# Revit family: LED SERIES
name_source: partatom
category: Lighting Fixtures
units: mm (PartAtom-declared; Revit-internal decimal feet)

## family parameters
Cut with Voids When Loaded = No
Host = Face
Light Source = Yes
OmniClass Number = 23.80.70.11
OmniClass Title = Luminaries for Internal Lighting
Part Type = Normal
Room Calculation Point = No
Round Connector Dimension = Use Diameter
Shared = No

## types (1)
- LED SERIES
    Color Filter = 16777215
    Default Elevation = 48"
    Description = Formed aluminum exit sign for light industrial or commercial applications.
    Dimming Lamp Color Temperature Shift = <None>
    Emit Shape Visible in Rendering = No
    Emit from Circle Diameter = 5"
    Finish = Black
    Finish2 = White
    Green = Green
    Lamp = Two
    Lettering = Red
    Light Source Symbol Size = 1"
    Manufacturer = Lifeshield
    Model = LED SERIES
    Opal lens = Etched Glass
    URL = https://www.currentlighting.com
    Wattage Comments = 5W

## geometry (parser evidence)
native form markers: Blend x1, Sweep x5
no freeform markers — native parametric forms only
